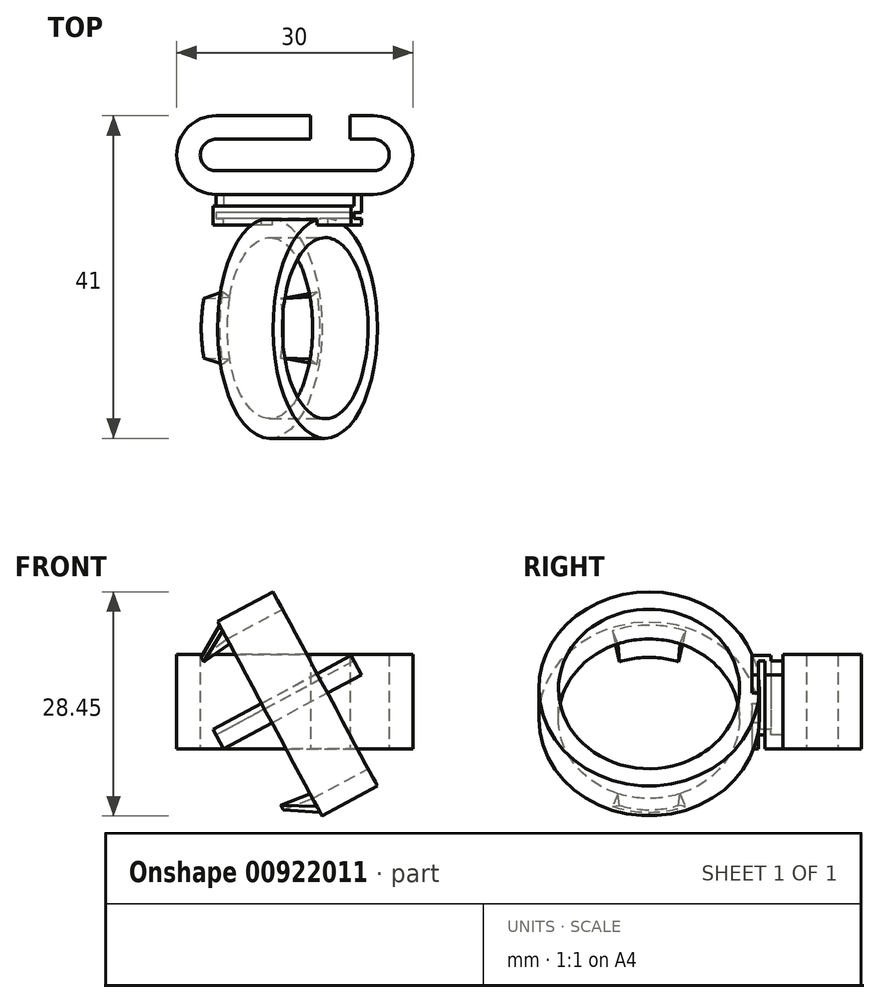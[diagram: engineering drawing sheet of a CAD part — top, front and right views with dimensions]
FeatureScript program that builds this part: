
annotation { "Feature Type Name" : "Feature", "Feature Type Description" : "" }
export const myFeature = defineFeature(function(context is Context, id is Id, definition is map)
    precondition{}
    {
        {
            var Q0;
            Q0=qCreatedBy(makeId("Top.planeOp"),FACE);
            var sketch = newSketch(context, id + "F0", { "sketchPlane" : qUnion([Q0])});
            skLineSegment(sketch, "E0", {"start": v(-20, 0) * mm, "end": v(0, 0) * mm});
            skArc(sketch, "E1", {"start": v(-20, 0) * mm, "mid": v(-22, 2) * mm, "end": v(-20, 4) * mm});
            skArc(sketch, "E2", {"start": v(0, 0) * mm, "mid": v(2, 2) * mm, "end": v(0, 4) * mm});
            skLineSegment(sketch, "E3", {"start": v(0, 4) * mm, "end": v(-3, 4) * mm});
            skLineSegment(sketch, "E4", {"start": v(-20, 4) * mm, "end": v(-8, 4) * mm});
            skLineSegment(sketch, "E5", {"start": v(-8, 4) * mm, "end": v(-8, 7) * mm});
            skLineSegment(sketch, "E6", {"start": v(-8, 7) * mm, "end": v(-20, 7) * mm});
            skLineSegment(sketch, "E7", {"start": v(-3, 4) * mm, "end": v(-3, 7) * mm});
            skLineSegment(sketch, "E8", {"start": v(-3, 7) * mm, "end": v(0, 7) * mm});
            skLineSegment(sketch, "E9", {"start": v(0, -3) * mm, "end": v(-20, -3) * mm});
            skArc(sketch, "E10", {"start": v(-20, -3) * mm, "mid": v(-25, 2) * mm, "end": v(-20, 7) * mm});
            skArc(sketch, "E11", {"start": v(0, -3) * mm, "mid": v(5, 2) * mm, "end": v(0, 7) * mm});
            skSolve(sketch);
        }
        {
            var Q0;
            Q0=makeQuery(id+"F0.imprint","IMPRINT",FACE,{"disambiguationData":[TD([[makeQuery(id+"F0.imprint","IMPRINT",EDGE,{"derivedFrom":sQuery(id+"F0.wireOp",EDGE,"E0")}),-1.0]])]});
            extrude(context, id + "F1", {"entities" : qUnion([Q0]), "depth" : 12 * mm, "offsetDistance" : 25 * mm});
        }
        {
            var Q0;
            Q0=makeQuery(id+"F1.opExtrude","SWEPT_FACE",FACE,{"disambiguationData":[OSD([sQuery(id+"F0.wireOp",EDGE,"E9")])]});
            var sketch = newSketch(context, id + "F2", { "sketchPlane" : qUnion([Q0])});
            skLineSegment(sketch, "E12", {"start": v(-20, 1.76) * mm, "end": v(-19.05, 0) * mm});
            skLineSegment(sketch, "E13", {"start": v(-19.05, 0) * mm, "end": v(0, 10.24) * mm});
            skLineSegment(sketch, "E14", {"start": v(0, 10.24) * mm, "end": v(-0.95, 12) * mm});
            skLineSegment(sketch, "E15", {"start": v(-0.95, 12) * mm, "end": v(-20, 1.76) * mm});
            skSolve(sketch);
        }
        {
            var Q0;
            Q0=sQuery(id+"F2.wireOp",EDGE,"E12");
            cPlane(context, id + "F3", {"entities" : qUnion([Q0]), "cplaneType" : CPlaneType.LINE_ANGLE, "offset" : 25 * mm, "angle" : 0 * degree, "oppositeDirection" : true, "width" : 150 * mm, "height" : 150 * mm});
        }
        {
            var Q0;
            Q0=qCreatedBy(id+"F3.planeOp",FACE);
            var sketch = newSketch(context, id + "F4", { "sketchPlane" : qUnion([Q0])});
            skLineSegment(sketch, "E16", {"start": v(3, 9.02) * mm, "end": v(5.3, 9.02) * mm});
            skLineSegment(sketch, "E17", {"start": v(3, 11.02) * mm, "end": v(4.5, 11.02) * mm});
            skLineSegment(sketch, "E18", {"start": v(4.5, 11.02) * mm, "end": v(4.5, 11.82) * mm});
            skLineSegment(sketch, "E19", {"start": v(4.5, 11.82) * mm, "end": v(6.9, 11.82) * mm});
            skLineSegment(sketch, "E20", {"start": v(6.9, 11.82) * mm, "end": v(6.9, 9.02) * mm});
            skLineSegment(sketch, "E21", {"start": v(6.9, 9.02) * mm, "end": v(6.1, 9.02) * mm});
            skLineSegment(sketch, "E22", {"start": v(5.3, 9.02) * mm, "end": v(5.3, 11.02) * mm});
            skLineSegment(sketch, "E23", {"start": v(5.3, 11.02) * mm, "end": v(6.1, 11.02) * mm});
            skLineSegment(sketch, "E24", {"start": v(6.1, 11.02) * mm, "end": v(6.1, 9.02) * mm});
            skLineSegment(sketch, "E25", {"start": v(3, 9.02) * mm, "end": v(3, 11.02) * mm});
            skSolve(sketch);
        }
        {
            var Q0;
            Q0=qSketchRegion(id+"F4",true);
            extrude(context, id + "F5", {"entities" : qUnion([Q0]), "operationType" : NewBodyOperationType.ADD, "oppositeDirection" : true, "depth" : 19.9 * mm, "offsetDistance" : 25 * mm});
        }
        {
            var Q0;
            Q0=qCreatedBy(id+"F3.planeOp",FACE);
            cPlane(context, id + "F6", {"entities" : qUnion([Q0]), "cplaneType" : CPlaneType.OFFSET, "offset" : 15 * mm, "oppositeDirection" : true, "width" : 150 * mm, "height" : 150 * mm});
        }
        {
            var Q0;
            Q0=qCreatedBy(id+"F6.planeOp",FACE);
            var sketch = newSketch(context, id + "F7", { "sketchPlane" : qUnion([Q0])});
            skLineSegment(sketch, "E26", {"start": v(6.9, 19.71) * mm, "end": v(6.9, -1.69) * mm});
            skCircle(sketch, "E27", {"center": v(20, 9.62) * mm, "radius": 11.5 * mm});
            skCircle(sketch, "E28", {"center": v(20, 9.62) * mm, "radius": 14 * mm});
            skSolve(sketch);
        }
        {
            var Q0;
            Q0=makeQuery(id+"F7.imprint","IMPRINT",FACE,{"disambiguationData":[TD([[makeQuery(id+"F7.imprint","IMPRINT",EDGE,{"derivedFrom":sQuery(id+"F7.wireOp",EDGE,"E27")}),-1.0]])]});
            var Q1;
            {var subQ0=sQuery(id+"F7.wireOp",EDGE,"E28");var subQ1=sQuery(id+"F7.wireOp",EDGE,"E26");var subQ2=makeQuery(id+"F7.imprint","INTERSECT",VERTEX,{"disambiguationData":[OD(0.0)],"derivedFrom":[subQ1,subQ0]});Q1=makeQuery(id+"F7.imprint","IMPRINT",FACE,{"disambiguationData":[TD([[makeQuery(id+"F7.imprint","IMPRINT",EDGE,{"disambiguationData":[TD([[subQ2,-1.0]])],"derivedFrom":subQ1}),-1.0]])]});}
            extrude(context, id + "F8", {"entities" : qUnion([Q0, Q1]), "operationType" : NewBodyOperationType.ADD, "depth" : 8 * mm, "offsetDistance" : 25 * mm});
        }
        {
            var Q0;
            Q0=qCreatedBy(makeId("Front.planeOp"),FACE);
            cPlane(context, id + "F9", {"entities" : qUnion([Q0]), "cplaneType" : CPlaneType.OFFSET, "offset" : 20 * mm, "width" : 150 * mm, "height" : 150 * mm});
        }
        {
            var Q0;
            Q0=qCreatedBy(id+"F9.planeOp",FACE);
            var sketch = newSketch(context, id + "F10", { "sketchPlane" : qUnion([Q0])});
            skLineSegment(sketch, "E29.0", {"start": v(-7.73, -6.28) * mm, "end": v(-18.62, 13.98) * mm});
            skPoint(sketch, "E30", {"position": v(-13.17, 3.85) * mm});
            skLineSegment(sketch, "E31", {"start": v(-13.17, 3.85) * mm, "end": v(-17.55, 1.5) * mm});
            skLineSegment(sketch, "E32", {"start": v(-7.73, -6.28) * mm, "end": v(-6.8, -8.03) * mm});
            skLineSegment(sketch, "E33", {"start": v(-6.8, -8.03) * mm, "end": v(-11.46, -7.72) * mm});
            skLineSegment(sketch, "E34", {"start": v(-11.46, -7.72) * mm, "end": v(-7.73, -6.28) * mm});
            skLineSegment(sketch, "E35.MirrorCS", {"start": v(-21.88, 11.66) * mm, "end": v(-18.62, 13.98) * mm});
            skLineSegment(sketch, "E36.MirrorCS", {"start": v(-19.55, 15.72) * mm, "end": v(-21.88, 11.66) * mm});
            skLineSegment(sketch, "E37.MirrorCS", {"start": v(-18.62, 13.98) * mm, "end": v(-19.55, 15.72) * mm});
            skSolve(sketch);
        }
        {
            var Q0;
            Q0=makeQuery(id+"F10.imprint","IMPRINT",FACE,{"disambiguationData":[TD([[makeQuery(id+"F10.imprint","IMPRINT",EDGE,{"derivedFrom":sQuery(id+"F10.wireOp",EDGE,"E32")}),-1.0]])]});
            var Q1;
            Q1=makeQuery(id+"F10.imprint","IMPRINT",FACE,{"disambiguationData":[TD([[makeQuery(id+"F10.imprint","IMPRINT",EDGE,{"derivedFrom":sQuery(id+"F10.wireOp",EDGE,"E35.MirrorCS")}),1.0]])]});
            var Q2;
            Q2=sQuery(id+"F10.wireOp",EDGE,"E31");
            revolve(context, id + "F11", {"operationType" : NewBodyOperationType.ADD, "surfaceOperationType" : NewSurfaceOperationType.NEW, "entities" : qUnion([Q0, Q1]), "axis" : qUnion([Q2]), "revolveType" : RevolveType.SYMMETRIC, "angle" : 40 * degree});
        }
    });
